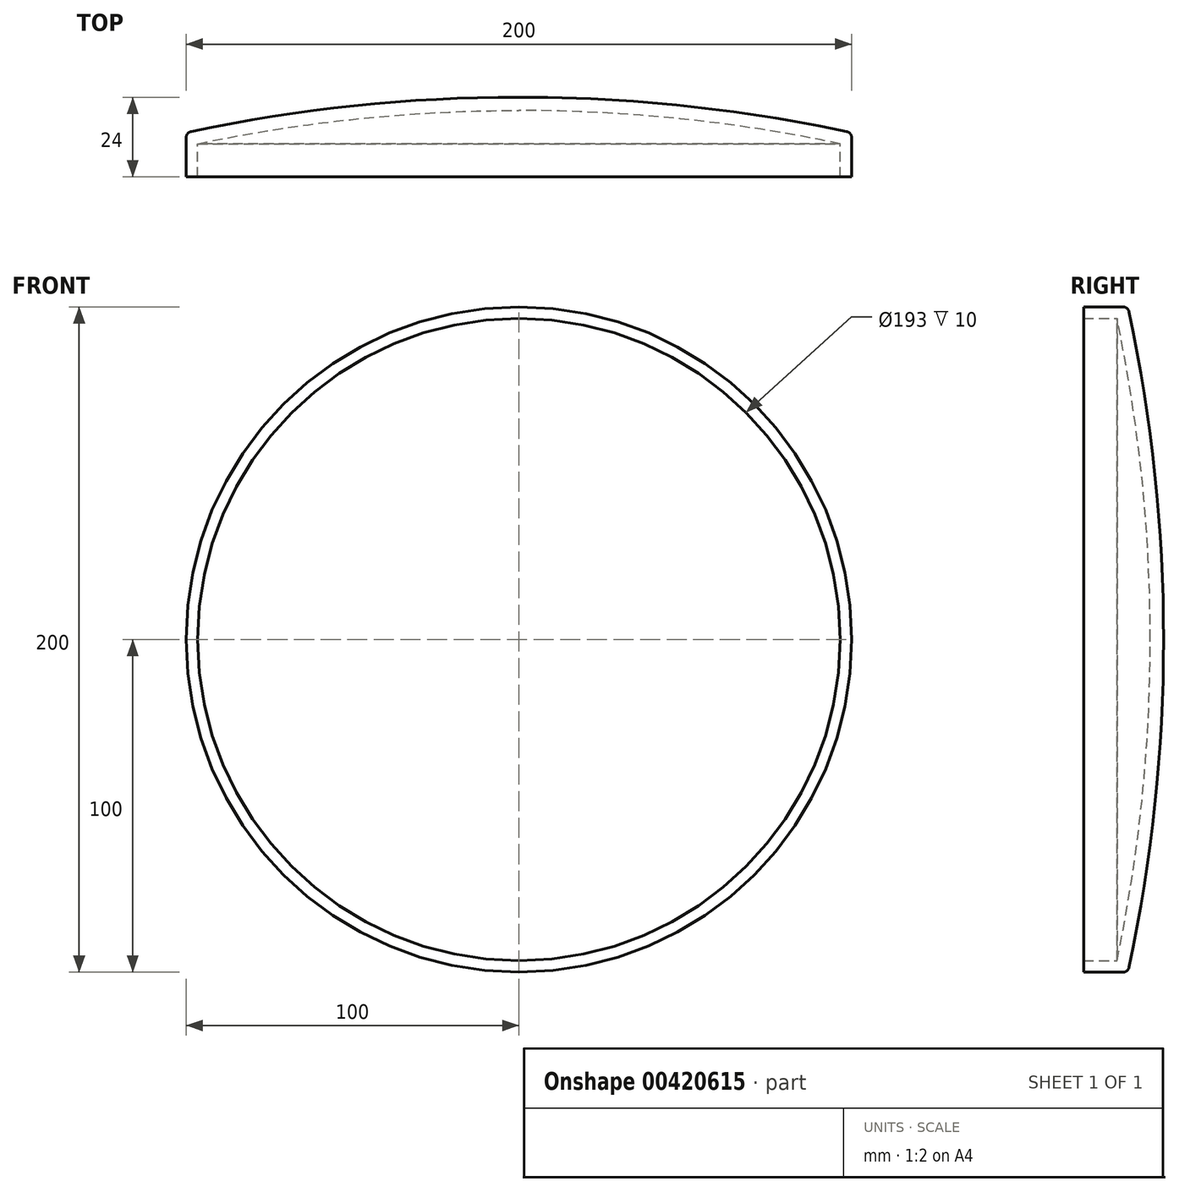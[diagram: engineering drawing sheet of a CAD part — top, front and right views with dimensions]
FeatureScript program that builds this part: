
annotation { "Feature Type Name" : "Feature", "Feature Type Description" : "" }
export const myFeature = defineFeature(function(context is Context, id is Id, definition is map)
    precondition{}
    {
        {
            var Q0;
            Q0=qCreatedBy(makeId("Top.planeOp"),FACE);
            var sketch = newSketch(context, id + "F0", { "sketchPlane" : qUnion([Q0])});
            skLineSegment(sketch, "E0", {"start": v(-96.5, -10) * mm, "end": v(-96.5, -20) * mm});
            skLineSegment(sketch, "E1", {"start": v(-96.5, -20) * mm, "end": v(-100, -20) * mm});
            skLineSegment(sketch, "E2", {"start": v(-100, -20) * mm, "end": v(-100, -6.65) * mm});
            skArc(sketch, "E3", {"start": v(0, 0) * mm, "mid": v(-48.5, -2.5) * mm, "end": v(-96.5, -10) * mm});
            skArc(sketch, "E4", {"start": v(0, 4) * mm, "mid": v(-50.28, 1.33) * mm, "end": v(-100, -6.65) * mm});
            skLineSegment(sketch, "E5", {"start": v(0, 4) * mm, "end": v(0, 0) * mm});
            skLineSegment(sketch, "E6", {"start": v(0, 0) * mm, "end": v(7.72, 0) * mm, "construction": true});
            skLineSegment(sketch, "E7", {"start": v(0, 0) * mm, "end": v(0, -10.13) * mm, "construction": true});
            skSolve(sketch);
        }
        {
            var Q0;
            Q0 = qSketchRegion(id + "F0", true);
            var Q1;
            Q1=sQuery(id+"F0.wireOp",EDGE,"E7");
            revolve(context, id + "F1", {"entities" : qUnion([Q0]), "axis" : qUnion([Q1]), "revolveType" : RevolveType.FULL});
        }
        {
            var Q0;
            Q0=makeQuery(id+"F1.opRevolve","SWEPT_EDGE",EDGE,{"disambiguationData":[OSD([sQuery(id+"F0.wireOp",EDGE,"E2"),sQuery(id+"F0.wireOp",EDGE,"E4")])]});
            fillet(context, id + "F2", {"entities" : qUnion([Q0]), "radius" : 2 * mm, "tangentPropagation" : true, "allowEdgeOverflow" : false});
        }
    });
